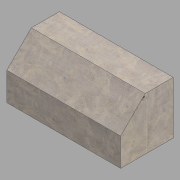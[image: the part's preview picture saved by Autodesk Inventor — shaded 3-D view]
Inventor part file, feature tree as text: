
AUTODESK INVENTOR PART (.ipt)
format: ipt  version: 2022.2 (Build 262287000, 287)  size: 130,048 bytes
history: native  units: in
note: dims shown in document units (in); Inventor stores cm internally (conversion verified against a paired STEP export)
features: extrude x1, sketch x1
ambient origin geometry x8: Origin, YZ Plane, XZ Plane, XY Plane, X Axis, Y Axis, Z Axis, Center Point
bodies: Solid1 (feature_tree)
feature tree (2):
  extrude  "Extrusion1"  Depth=7.5in
  sketch  "Sketch1"  dims[d0=7.5in d1=7.5in d2=4.0in d3=4.0in d4=3.5in d5=3.5in d6=16.25in d7=0.0in]
